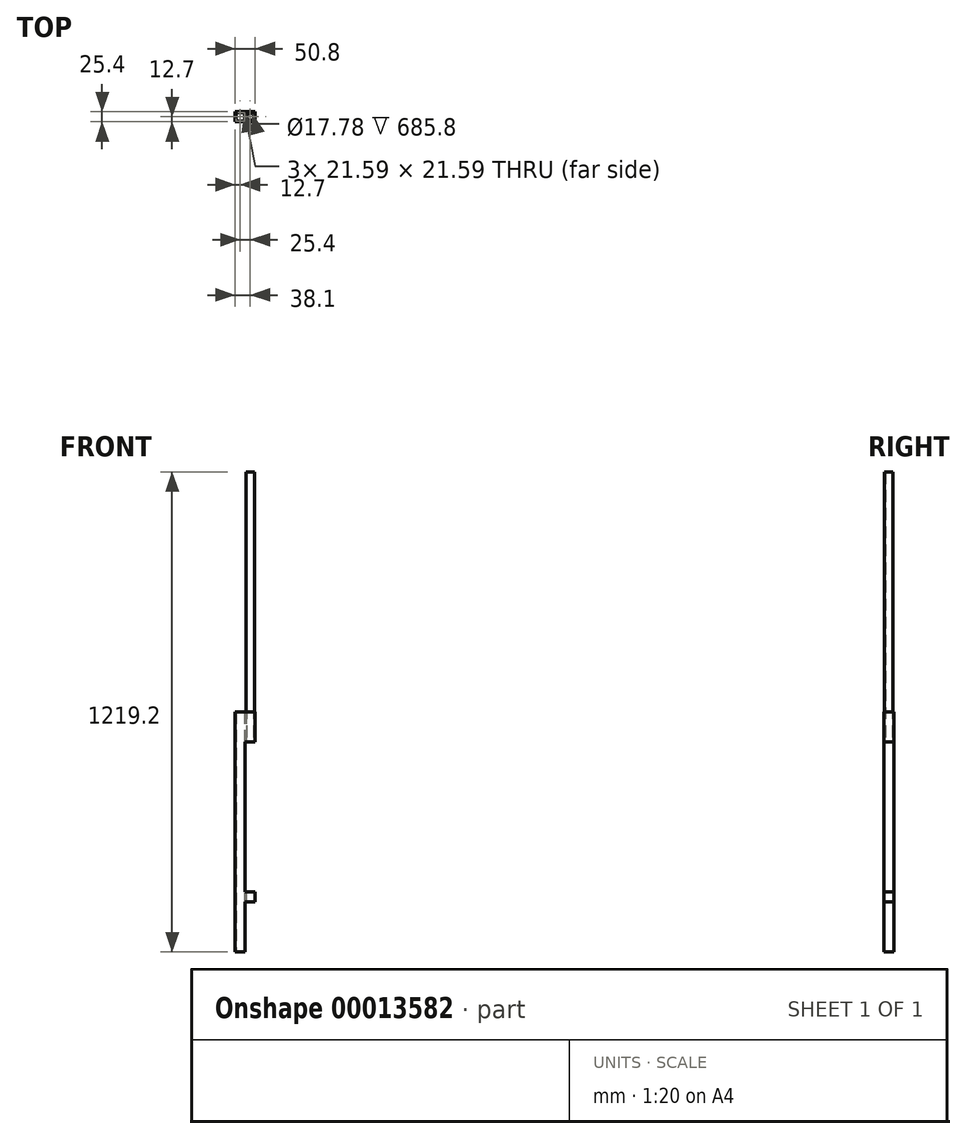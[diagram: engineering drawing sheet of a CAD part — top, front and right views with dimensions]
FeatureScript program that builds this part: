
annotation { "Feature Type Name" : "Feature", "Feature Type Description" : "" }
export const myFeature = defineFeature(function(context is Context, id is Id, definition is map)
    precondition{}
    {
        {
            var Q0;
            Q0=qCreatedBy(makeId("Top.planeOp"),FACE);
            var sketch = newSketch(context, id + "F0", { "sketchPlane" : qUnion([Q0])});
            skLineSegment(sketch, "E0.bottom", {"start": v(12.7, 12.7) * mm, "end": v(-12.7, 12.7) * mm});
            skLineSegment(sketch, "E0.top", {"start": v(12.7, -12.7) * mm, "end": v(-12.7, -12.7) * mm});
            skLineSegment(sketch, "E0.left", {"start": v(12.7, 12.7) * mm, "end": v(12.7, -12.7) * mm});
            skLineSegment(sketch, "E0.right", {"start": v(-12.7, 12.7) * mm, "end": v(-12.7, -12.7) * mm});
            skPoint(sketch, "E0.middle", {"position": v(0, 0) * mm});
            skLineSegment(sketch, "E1.bottom", {"start": v(10.8, 10.8) * mm, "end": v(-10.8, 10.8) * mm});
            skLineSegment(sketch, "E1.top", {"start": v(10.8, -10.8) * mm, "end": v(-10.8, -10.8) * mm});
            skLineSegment(sketch, "E1.left", {"start": v(10.8, 10.8) * mm, "end": v(10.8, -10.8) * mm});
            skLineSegment(sketch, "E1.right", {"start": v(-10.8, 10.8) * mm, "end": v(-10.8, -10.8) * mm});
            skLineSegment(sketch, "E2.bottom", {"start": v(12.7, 12.7) * mm, "end": v(38.1, 12.7) * mm});
            skLineSegment(sketch, "E2.top", {"start": v(12.7, -12.7) * mm, "end": v(38.1, -12.7) * mm});
            skLineSegment(sketch, "E2.right", {"start": v(38.1, 12.7) * mm, "end": v(38.1, -12.7) * mm});
            skLineSegment(sketch, "E3.bottom", {"start": v(14.6, 10.8) * mm, "end": v(36.2, 10.8) * mm});
            skLineSegment(sketch, "E3.top", {"start": v(14.6, -10.8) * mm, "end": v(36.2, -10.8) * mm});
            skLineSegment(sketch, "E3.left", {"start": v(14.6, 10.8) * mm, "end": v(14.6, -10.8) * mm});
            skLineSegment(sketch, "E3.right", {"start": v(36.2, 10.8) * mm, "end": v(36.2, -10.8) * mm});
            skLineSegment(sketch, "E4", {"start": v(25.4, 12.7) * mm, "end": v(25.4, 10.8) * mm, "construction": true});
            skLineSegment(sketch, "E5", {"start": v(25.4, -10.8) * mm, "end": v(25.4, -12.7) * mm, "construction": true});
            skSolve(sketch);
        }
        {
            var Q0;
            Q0 = qSketchRegion(id + "F0", true);
            extrude(context, id + "F1", {"entities" : qUnion([Q0]), "depth" : 609.6 * mm});
        }
        {
            var Q0;
            Q0=makeQuery(id+"F1.opExtrude","SWEPT_FACE",FACE,{"disambiguationData":[OSD([sQuery(id+"F0.wireOp",EDGE,"E2.right")])]});
            var sketch = newSketch(context, id + "F2", { "sketchPlane" : qUnion([Q0])});
            skLineSegment(sketch, "E6.bottom", {"start": v(-12.7, 0) * mm, "end": v(12.7, 0) * mm});
            skLineSegment(sketch, "E6.top", {"start": v(-12.7, 127) * mm, "end": v(12.7, 127) * mm});
            skLineSegment(sketch, "E6.left", {"start": v(-12.7, 0) * mm, "end": v(-12.7, 127) * mm});
            skLineSegment(sketch, "E6.right", {"start": v(12.7, 0) * mm, "end": v(12.7, 127) * mm});
            skLineSegment(sketch, "E7.bottom", {"start": v(-12.7, 152.4) * mm, "end": v(12.7, 152.4) * mm});
            skLineSegment(sketch, "E7.top", {"start": v(-12.7, 533.4) * mm, "end": v(12.7, 533.4) * mm});
            skLineSegment(sketch, "E7.left", {"start": v(-12.7, 152.4) * mm, "end": v(-12.7, 533.4) * mm});
            skLineSegment(sketch, "E7.right", {"start": v(12.7, 152.4) * mm, "end": v(12.7, 533.4) * mm});
            skSolve(sketch);
        }
        {
            var Q0;
            Q0 = qSketchRegion(id + "F2", true);
            extrude(context, id + "F3", {"entities" : qUnion([Q0]), "operationType" : NewBodyOperationType.REMOVE, "oppositeDirection" : true, "depth" : 25.4 * mm});
        }
        {
            var Q0;
            Q0=makeQuery(id+"F3.boolean.opBoolean","COPY",FACE,{"derivedFrom":makeQuery(id+"F3.opExtrude","SWEPT_FACE",FACE,{"disambiguationData":[OSD([sQuery(id+"F2.wireOp",EDGE,"E7.top")])]})});
            var sketch = newSketch(context, id + "F4", { "sketchPlane" : qUnion([Q0])});
            skCircle(sketch, "E8", {"center": v(25.4, 0) * mm, "radius": 10.8 * mm});
            skCircle(sketch, "E9", {"center": v(25.4, 0) * mm, "radius": 8.9 * mm});
            skSolve(sketch);
        }
        {
            var Q0;
            Q0 = qSketchRegion(id + "F4", true);
            extrude(context, id + "F5", {"entities" : qUnion([Q0]), "oppositeDirection" : true, "depth" : 685.8 * mm});
        }
    });
